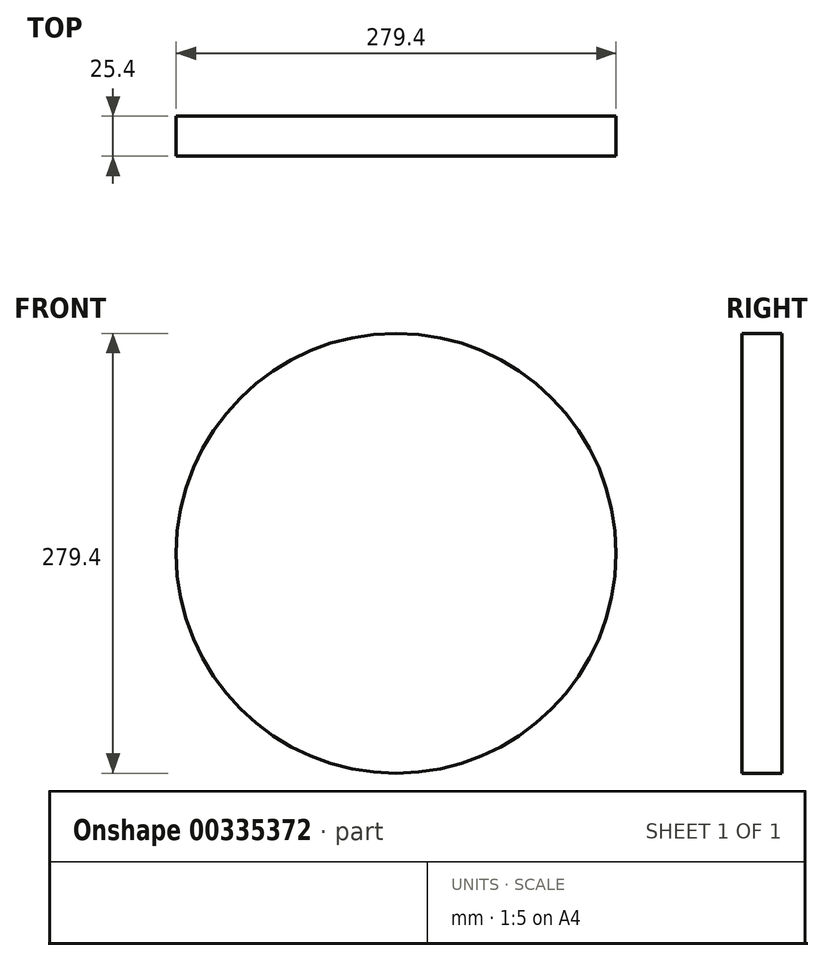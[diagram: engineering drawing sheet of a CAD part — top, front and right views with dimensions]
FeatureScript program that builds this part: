
annotation { "Feature Type Name" : "Feature", "Feature Type Description" : "" }
export const myFeature = defineFeature(function(context is Context, id is Id, definition is map)
    precondition{}
    {
        {
            var Q0;
            Q0=qCreatedBy(makeId("Front.planeOp"),FACE);
            var sketch = newSketch(context, id + "F0", { "sketchPlane" : qUnion([Q0])});
            skCircle(sketch, "E0", {"center": v(0, 0) * mm, "radius": 139.7 * mm});
            skSolve(sketch);
        }
        {
            var Q0;
            Q0=makeQuery(id+"F0.imprint","IMPRINT",FACE,{"disambiguationData":[TD([[makeQuery(id+"F0.imprint","IMPRINT",EDGE,{"derivedFrom":sQuery(id+"F0.wireOp",EDGE,"E0")}),1.0]])]});
            extrude(context, id + "F1", {"entities" : qUnion([Q0]), "depth" : 25.4 * mm});
        }
    });
